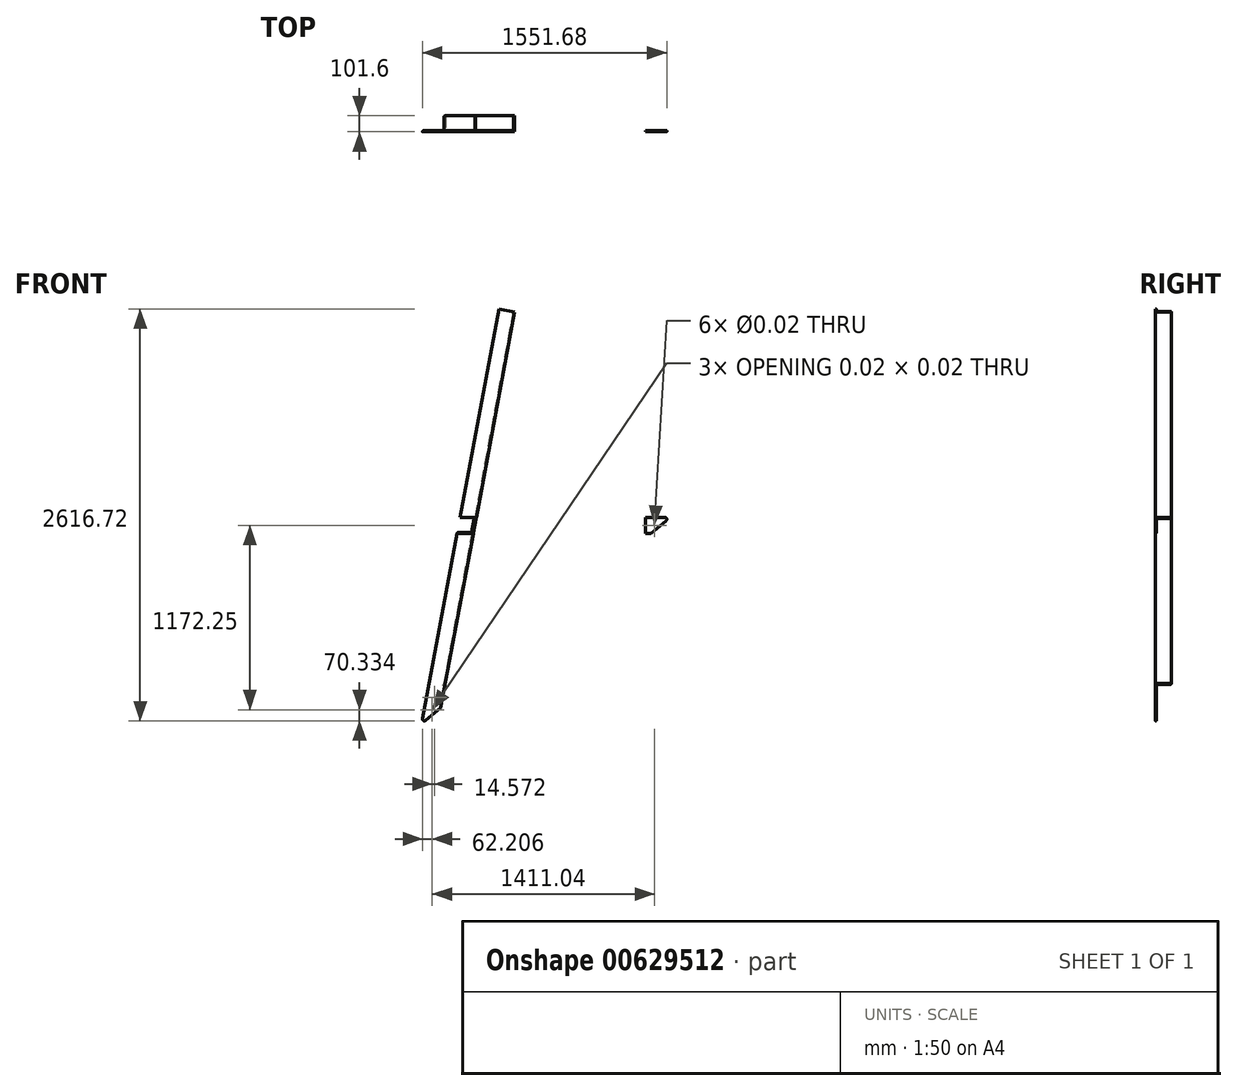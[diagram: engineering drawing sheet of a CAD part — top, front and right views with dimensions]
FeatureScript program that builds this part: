
annotation { "Feature Type Name" : "Feature", "Feature Type Description" : "" }
export const myFeature = defineFeature(function(context is Context, id is Id, definition is map)
    precondition{}
    {
        {
            var Q0;
            Q0=qCreatedBy(makeId("Front.planeOp"),FACE);
            var sketch = newSketch(context, id + "F0", { "sketchPlane" : qUnion([Q0])});
            skLineSegment(sketch, "E0", {"start": v(-1073.2, 0) * mm, "end": v(1073.2, 0) * mm, "construction": true});
            skLineSegment(sketch, "E1", {"start": v(-196.73, -1055.02) * mm, "end": v(196.73, 1055.02) * mm, "construction": true});
            skLineSegment(sketch, "E2", {"start": v(-1073.2, 0) * mm, "end": v(-196.73, -1055.02) * mm, "construction": true});
            skLineSegment(sketch, "E3", {"start": v(1073.2, 0) * mm, "end": v(-196.73, -1055.02) * mm, "construction": true});
            skLineSegment(sketch, "E4", {"start": v(1073.2, 0) * mm, "end": v(196.73, 1055.02) * mm, "construction": true});
            skLineSegment(sketch, "E5", {"start": v(-1073.2, 0) * mm, "end": v(196.73, 1055.02) * mm, "construction": true});
            skSolve(sketch);
        }
        {
            var Q0;
            Q0=sQuery(id+"F0.wireOp",VERTEX,"E3.start");
            var Q1;
            Q1=qCreatedBy(makeId("Right.planeOp"),FACE);
            cPlane(context, id + "F1", {"entities" : qUnion([Q0, Q1]), "cplaneType" : CPlaneType.PLANE_POINT, "offset" : 25.4 * mm, "width" : 152.4 * mm, "height" : 152.4 * mm});
        }
        {
            var Q0;
            Q0=qCreatedBy(id+"F1.planeOp",FACE);
            var sketch = newSketch(context, id + "F2", { "sketchPlane" : qUnion([Q0])});
            skLineSegment(sketch, "E6", {"start": v(-77.3, 0) * mm, "end": v(77.3, 0) * mm, "construction": true});
            skSolve(sketch);
        }
        {
            var Q0;
            Q0=qCreatedBy(id+"F1.planeOp",FACE);
            var sketch = newSketch(context, id + "F3", { "sketchPlane" : qUnion([Q0])});
            skLineSegment(sketch, "E7", {"start": v(0, 0) * mm, "end": v(101.6, 0) * mm});
            skLineSegment(sketch, "E8", {"start": v(101.6, 0) * mm, "end": v(101.6, -0.76) * mm});
            skLineSegment(sketch, "E9", {"start": v(96.01, -6.35) * mm, "end": v(11.94, -6.35) * mm});
            skLineSegment(sketch, "E10", {"start": v(6.35, -11.94) * mm, "end": v(6.35, -96.01) * mm});
            skLineSegment(sketch, "E11", {"start": v(0.76, -101.6) * mm, "end": v(0, -101.6) * mm});
            skLineSegment(sketch, "E12", {"start": v(0, -101.6) * mm, "end": v(0, 0) * mm});
            skPoint(sketch, "E13.visualSharp", {"position": v(6.35, -101.6) * mm});
            skArc(sketch, "E13.filletArc", {"start": v(0.76, -101.6) * mm, "mid": v(4.71, -99.96) * mm, "end": v(6.35, -96.01) * mm});
            skPoint(sketch, "E14.visualSharp", {"position": v(101.6, -6.35) * mm});
            skArc(sketch, "E14.filletArc", {"start": v(96.01, -6.35) * mm, "mid": v(99.96, -4.71) * mm, "end": v(101.6, -0.76) * mm});
            skPoint(sketch, "E15.visualSharp", {"position": v(6.35, -6.35) * mm});
            skArc(sketch, "E15.filletArc", {"start": v(11.94, -6.35) * mm, "mid": v(7.99, -7.99) * mm, "end": v(6.35, -11.94) * mm});
            skSolve(sketch);
        }
        {
            var Q0;
            Q0=makeQuery(id+"F3.imprint","IMPRINT",FACE,{"disambiguationData":[TD([[makeQuery(id+"F3.imprint","IMPRINT",EDGE,{"derivedFrom":sQuery(id+"F3.wireOp",EDGE,"E7")}),-1.0]])]});
            var Q1;
            Q1=sQuery(id+"F0.wireOp",VERTEX,"E0.start");
            extrude(context, id + "F4", {"entities" : qUnion([Q0]), "oppositeDirection" : true, "endBoundEntityVertex" : qUnion([Q1]), "depth" : 2540 * mm, "hasSecondDirection" : true, "secondDirectionOppositeDirection" : false, "secondDirectionDepth" : 254 * mm});
        }
        {
            var Q0;
            Q0=sQuery(id+"F0.wireOp",VERTEX,"E5.end");
            var Q1;
            Q1=sQuery(id+"F0.wireOp",EDGE,"E1");
            cPlane(context, id + "F5", {"entities" : qUnion([Q0, Q1]), "cplaneType" : CPlaneType.LINE_POINT, "offset" : 25.4 * mm, "width" : 152.4 * mm, "height" : 152.4 * mm});
        }
        {
            var Q0;
            Q0=qCreatedBy(id+"F5.planeOp",FACE);
            var sketch = newSketch(context, id + "F6", { "sketchPlane" : qUnion([Q0])});
            skLineSegment(sketch, "E16", {"start": v(0, 0) * mm, "end": v(0, 101.6) * mm});
            skLineSegment(sketch, "E17", {"start": v(0, 101.6) * mm, "end": v(-0.76, 101.6) * mm});
            skLineSegment(sketch, "E18", {"start": v(-6.35, 96.01) * mm, "end": v(-6.35, 11.94) * mm});
            skLineSegment(sketch, "E19", {"start": v(-11.94, 6.35) * mm, "end": v(-96.01, 6.35) * mm});
            skLineSegment(sketch, "E20", {"start": v(-101.6, 0.76) * mm, "end": v(-101.6, 0) * mm});
            skLineSegment(sketch, "E21", {"start": v(0, 0) * mm, "end": v(-101.6, 0) * mm});
            skPoint(sketch, "E22.visualSharp", {"position": v(-6.35, 101.6) * mm});
            skArc(sketch, "E22.filletArc", {"start": v(-0.76, 101.6) * mm, "mid": v(-4.71, 99.96) * mm, "end": v(-6.35, 96.01) * mm});
            skPoint(sketch, "E23.visualSharp", {"position": v(-6.35, 6.35) * mm});
            skArc(sketch, "E23.filletArc", {"start": v(-11.94, 6.35) * mm, "mid": v(-7.99, 7.99) * mm, "end": v(-6.35, 11.94) * mm});
            skPoint(sketch, "E24.visualSharp", {"position": v(-101.6, 6.35) * mm});
            skArc(sketch, "E24.filletArc", {"start": v(-96.01, 6.35) * mm, "mid": v(-99.96, 4.71) * mm, "end": v(-101.6, 0.76) * mm});
            skSolve(sketch);
        }
        {
            var Q0;
            Q0=makeQuery(id+"F6.imprint","IMPRINT",FACE,{"disambiguationData":[TD([[makeQuery(id+"F6.imprint","IMPRINT",EDGE,{"derivedFrom":sQuery(id+"F6.wireOp",EDGE,"E16")}),1.0]])]});
            extrude(context, id + "F7", {"entities" : qUnion([Q0]), "oppositeDirection" : true, "depth" : 2540 * mm, "hasSecondDirection" : true, "secondDirectionOppositeDirection" : false, "secondDirectionDepth" : 254 * mm});
        }
        {
            var Q0;
            Q0=qSketchRegion(id+"F3",true);
            extrude(context, id + "F8", {"entities" : qUnion([Q0]), "operationType" : NewBodyOperationType.REMOVE, "endBound" : BoundingType.THROUGH_ALL, "oppositeDirection" : true, "depth" : 25.4 * mm});
        }
        {
            var Q0;
            Q0=makeQuery(id+"F4.opExtrude","SWEPT_FACE",FACE,{"disambiguationData":[OSD([sQuery(id+"F3.wireOp",EDGE,"E10")])]});
            var sketch = newSketch(context, id + "F9", { "sketchPlane" : qUnion([Q0])});
            skLineSegment(sketch, "E25", {"start": v(-877.83, -162.31) * mm, "end": v(-1268.58, 162.31) * mm});
            skLineSegment(sketch, "E26", {"start": v(-1268.58, 162.31) * mm, "end": v(-1333.5, 84.16) * mm});
            skLineSegment(sketch, "E27", {"start": v(-1333.5, 84.16) * mm, "end": v(-942.76, -240.46) * mm});
            skLineSegment(sketch, "E28", {"start": v(-942.76, -240.46) * mm, "end": v(-877.83, -162.31) * mm});
            skSolve(sketch);
        }
        {
            var Q0;
            Q0=qSketchRegion(id+"F9",true);
            extrude(context, id + "F10", {"entities" : qUnion([Q0]), "operationType" : NewBodyOperationType.REMOVE, "endBound" : BoundingType.THROUGH_ALL, "depth" : 25.4 * mm});
        }
        {
            var Q0;
            Q0=makeQuery(id+"F4.opExtrude","SWEPT_FACE",FACE,{"disambiguationData":[OSD([sQuery(id+"F3.wireOp",EDGE,"E12")])]});
            var sketch = newSketch(context, id + "F11", { "sketchPlane" : qUnion([Q0])});
            skLineSegment(sketch, "E29", {"start": v(1333.5, 84.16) * mm, "end": v(942.76, -240.46) * mm});
            skLineSegment(sketch, "E30", {"start": v(942.76, -240.46) * mm, "end": v(1072.6, -396.76) * mm});
            skLineSegment(sketch, "E31", {"start": v(1072.6, -396.76) * mm, "end": v(1463.35, -72.14) * mm});
            skLineSegment(sketch, "E32", {"start": v(1463.35, -72.14) * mm, "end": v(1333.5, 84.16) * mm});
            skSolve(sketch);
        }
        {
            var Q0;
            Q0=qSketchRegion(id+"F11",true);
            extrude(context, id + "F12", {"entities" : qUnion([Q0]), "operationType" : NewBodyOperationType.REMOVE, "endBound" : BoundingType.THROUGH_ALL, "oppositeDirection" : true, "depth" : 25.4 * mm});
        }
        {
            var Q0;
            Q0=makeQuery(id+"F10.boolean.opBoolean","MERGE",FACE,{"derivedFrom":[makeQuery(id+"F4.opExtrude","SWEPT_FACE",FACE,{"disambiguationData":[OSD([sQuery(id+"F3.wireOp",EDGE,"E10")])]}),makeQuery(id+"F10.opExtrude","CAP_FACE",FACE,{"disambiguationData":[OSD([sQuery(id+"F9.wireOp",EDGE,"E25"),sQuery(id+"F9.wireOp",EDGE,"E26"),sQuery(id+"F9.wireOp",EDGE,"E27"),sQuery(id+"F9.wireOp",EDGE,"E28")])],"isStart":true})]});
            var sketch = newSketch(context, id + "F13", { "sketchPlane" : qUnion([Q0])});
            skLineSegment(sketch, "E33", {"start": v(-1131.3, -50.8) * mm, "end": v(-1051.8, -50.8) * mm, "construction": true});
            skSolve(sketch);
        }
        {
            var Q0;
            Q0=sQuery(id+"F13.wireOp",VERTEX,"E33.start");
            var Q1;
            Q1=sQuery(id+"F13.wireOp",VERTEX,"E33.end");
            var Q2;
            Q2=makeQuery(id+"F4.opExtrude","SWEPT_BODY",BODY,{"disambiguationData":[OSD([sQuery(id+"F3.wireOp",EDGE,"E7"),sQuery(id+"F3.wireOp",EDGE,"E8"),sQuery(id+"F3.wireOp",EDGE,"E9"),sQuery(id+"F3.wireOp",EDGE,"E10"),sQuery(id+"F3.wireOp",EDGE,"E11"),sQuery(id+"F3.wireOp",EDGE,"E12"),sQuery(id+"F3.wireOp",EDGE,"E13.filletArc"),sQuery(id+"F3.wireOp",EDGE,"E14.filletArc"),sQuery(id+"F3.wireOp",EDGE,"E15.filletArc")])]});
            var Q3;
            Q3=makeQuery(id+"F8.boolean.opBoolean","SPLIT",BODY,{"disambiguationData":[OD(0.0)],"derivedFrom":makeQuery(id+"F7.opExtrude","SWEPT_BODY",BODY,{"disambiguationData":[OSD([sQuery(id+"F6.wireOp",EDGE,"E16"),sQuery(id+"F6.wireOp",EDGE,"E17"),sQuery(id+"F6.wireOp",EDGE,"E18"),sQuery(id+"F6.wireOp",EDGE,"E19"),sQuery(id+"F6.wireOp",EDGE,"E20"),sQuery(id+"F6.wireOp",EDGE,"E21"),sQuery(id+"F6.wireOp",EDGE,"E22.filletArc"),sQuery(id+"F6.wireOp",EDGE,"E23.filletArc"),sQuery(id+"F6.wireOp",EDGE,"E24.filletArc")])]})});
            var Q4;
            Q4=makeQuery(id+"F8.boolean.opBoolean","SPLIT",BODY,{"disambiguationData":[OD(1.0)],"derivedFrom":makeQuery(id+"F7.opExtrude","SWEPT_BODY",BODY,{"disambiguationData":[OSD([sQuery(id+"F6.wireOp",EDGE,"E16"),sQuery(id+"F6.wireOp",EDGE,"E17"),sQuery(id+"F6.wireOp",EDGE,"E18"),sQuery(id+"F6.wireOp",EDGE,"E19"),sQuery(id+"F6.wireOp",EDGE,"E20"),sQuery(id+"F6.wireOp",EDGE,"E21"),sQuery(id+"F6.wireOp",EDGE,"E22.filletArc"),sQuery(id+"F6.wireOp",EDGE,"E23.filletArc"),sQuery(id+"F6.wireOp",EDGE,"E24.filletArc")])]})});
            hole(context, id + "F14", {"style" : HoleStyle.SIMPLE, "endStyle" : HoleEndStyle.THROUGH, "standardTappedOrClearance" : lookupTablePath({ "standard" : "ANSI", "size" : "9/16 (0.56)", "type" : "Drilled" }), "standardBlindInLast" : lookupTablePath({ "standard" : "ANSI", "size" : "9/16", "type" : "Drilled" }), "holeDiameter" : 9 / 406.4 * mm, "isTappedThrough" : true, "tappedDepth" : 12.7 * mm, "tapClearance" : 3, "locations" : qUnion([Q0, Q1]), "scope" : qUnion([Q2, Q3, Q4])});
        }
        {
            var Q0;
            Q0=sQuery(id+"F0.wireOp",EDGE,"E4");
            cPoint(context, id + "F15", {"entities" : qUnion([Q0]), "parameter" : 0.5});
        }
        {
            var Q0;
            Q0=qCreatedBy(id+"F15",VERTEX);
            var Q1;
            Q1=sQuery(id+"F0.wireOp",EDGE,"E4");
            cPlane(context, id + "F16", {"entities" : qUnion([Q0, Q1]), "cplaneType" : CPlaneType.LINE_POINT, "offset" : 25.4 * mm, "width" : 152.4 * mm, "height" : 152.4 * mm});
        }
        {
            var Q0;
            {var subQ2=sQuery(id+"F6.wireOp",EDGE,"E19");Q0=makeQuery(id+"F8.boolean.opBoolean","SPLIT",FACE,{"disambiguationData":[TD([makeQuery(id+"F8.opExtrude","SWEPT_FACE",FACE,{"disambiguationData":[OSD([sQuery(id+"F3.wireOp",EDGE,"E10")])]})])],"derivedFrom":makeQuery(id+"F7.opExtrude","SWEPT_FACE",FACE,{"disambiguationData":[OSD([subQ2])]})});}
            var sketch = newSketch(context, id + "F17", { "sketchPlane" : qUnion([Q0])});
            skLineSegment(sketch, "E34", {"start": v(196.73, -1055.02) * mm, "end": v(587.48, -1379.64) * mm});
            skLineSegment(sketch, "E35", {"start": v(587.48, -1379.64) * mm, "end": v(522.55, -1457.8) * mm});
            skLineSegment(sketch, "E36", {"start": v(522.55, -1457.8) * mm, "end": v(131.8, -1133.17) * mm});
            skLineSegment(sketch, "E37", {"start": v(131.8, -1133.17) * mm, "end": v(196.73, -1055.02) * mm});
            skSolve(sketch);
        }
        {
            var Q0;
            {var subQ1=sQuery(id+"F6.wireOp",EDGE,"E21");Q0=makeQuery(id+"F8.boolean.opBoolean","SPLIT",FACE,{"disambiguationData":[TD([makeQuery(id+"F8.opExtrude","SWEPT_FACE",FACE,{"disambiguationData":[OSD([sQuery(id+"F3.wireOp",EDGE,"E11")])]})])],"derivedFrom":makeQuery(id+"F7.opExtrude","SWEPT_FACE",FACE,{"disambiguationData":[OSD([subQ1])]})});}
            var sketch = newSketch(context, id + "F18", { "sketchPlane" : qUnion([Q0])});
            skLineSegment(sketch, "E38", {"start": v(-131.8, -1133.17) * mm, "end": v(-522.55, -1457.8) * mm});
            skLineSegment(sketch, "E39", {"start": v(-522.55, -1457.8) * mm, "end": v(-392.7, -1614.1) * mm});
            skLineSegment(sketch, "E40", {"start": v(-392.7, -1614.1) * mm, "end": v(-1.95, -1289.47) * mm});
            skLineSegment(sketch, "E41", {"start": v(-1.95, -1289.47) * mm, "end": v(-131.8, -1133.17) * mm});
            skSolve(sketch);
        }
        {
            var Q0;
            Q0=qSketchRegion(id+"F17",true);
            extrude(context, id + "F19", {"entities" : qUnion([Q0]), "operationType" : NewBodyOperationType.REMOVE, "endBound" : BoundingType.THROUGH_ALL, "depth" : 25.4 * mm});
        }
        {
            var Q0;
            Q0=qSketchRegion(id+"F18",true);
            extrude(context, id + "F20", {"entities" : qUnion([Q0]), "operationType" : NewBodyOperationType.REMOVE, "endBound" : BoundingType.THROUGH_ALL, "oppositeDirection" : true, "depth" : 25.4 * mm});
        }
        {
            var Q0;
            {var subQ2=sQuery(id+"F6.wireOp",EDGE,"E19");Q0=makeQuery(id+"F19.boolean.opBoolean","MERGE",FACE,{"derivedFrom":[makeQuery(id+"F8.boolean.opBoolean","SPLIT",FACE,{"disambiguationData":[TD([makeQuery(id+"F8.opExtrude","SWEPT_FACE",FACE,{"disambiguationData":[OSD([sQuery(id+"F3.wireOp",EDGE,"E10")])]})])],"derivedFrom":makeQuery(id+"F7.opExtrude","SWEPT_FACE",FACE,{"disambiguationData":[OSD([subQ2])]})}),makeQuery(id+"F19.opExtrude","CAP_FACE",FACE,{"disambiguationData":[OSD([sQuery(id+"F17.wireOp",EDGE,"E34"),sQuery(id+"F17.wireOp",EDGE,"E35"),sQuery(id+"F17.wireOp",EDGE,"E36"),sQuery(id+"F17.wireOp",EDGE,"E37")])],"isStart":true})]});}
            var sketch = newSketch(context, id + "F21", { "sketchPlane" : qUnion([Q0])});
            skLineSegment(sketch, "E42", {"start": v(279.73, -1223.05) * mm, "end": v(265.16, -1144.9) * mm, "construction": true});
            skSolve(sketch);
        }
        {
            var Q0;
            Q0=sQuery(id+"F21.wireOp",VERTEX,"E42.end");
            var Q1;
            Q1=sQuery(id+"F21.wireOp",VERTEX,"E42.start");
            var Q2;
            Q2=makeQuery(id+"F8.boolean.opBoolean","SPLIT",BODY,{"disambiguationData":[OD(1.0)],"derivedFrom":makeQuery(id+"F7.opExtrude","SWEPT_BODY",BODY,{"disambiguationData":[OSD([sQuery(id+"F6.wireOp",EDGE,"E16"),sQuery(id+"F6.wireOp",EDGE,"E17"),sQuery(id+"F6.wireOp",EDGE,"E18"),sQuery(id+"F6.wireOp",EDGE,"E19"),sQuery(id+"F6.wireOp",EDGE,"E20"),sQuery(id+"F6.wireOp",EDGE,"E21"),sQuery(id+"F6.wireOp",EDGE,"E22.filletArc"),sQuery(id+"F6.wireOp",EDGE,"E23.filletArc"),sQuery(id+"F6.wireOp",EDGE,"E24.filletArc")])]})});
            var Q3;
            Q3=makeQuery(id+"F4.opExtrude","SWEPT_BODY",BODY,{"disambiguationData":[OSD([sQuery(id+"F3.wireOp",EDGE,"E7"),sQuery(id+"F3.wireOp",EDGE,"E8"),sQuery(id+"F3.wireOp",EDGE,"E9"),sQuery(id+"F3.wireOp",EDGE,"E10"),sQuery(id+"F3.wireOp",EDGE,"E11"),sQuery(id+"F3.wireOp",EDGE,"E12"),sQuery(id+"F3.wireOp",EDGE,"E13.filletArc"),sQuery(id+"F3.wireOp",EDGE,"E14.filletArc"),sQuery(id+"F3.wireOp",EDGE,"E15.filletArc")])]});
            hole(context, id + "F22", {"style" : HoleStyle.SIMPLE, "endStyle" : HoleEndStyle.THROUGH, "standardTappedOrClearance" : lookupTablePath({ "standard" : "ANSI", "size" : "9/16 (0.56)", "type" : "Drilled" }), "standardBlindInLast" : lookupTablePath({ "standard" : "ANSI", "size" : "9/16", "type" : "Drilled" }), "holeDiameter" : 9 / 406.4 * mm, "isTappedThrough" : true, "tappedDepth" : 12.7 * mm, "tapClearance" : 3, "locations" : qUnion([Q0, Q1]), "scope" : qUnion([Q2, Q3])});
        }
        {
            var Q0;
            {var subQ2=sQuery(id+"F6.wireOp",EDGE,"E19");Q0=makeQuery(id+"F19.boolean.opBoolean","MERGE",FACE,{"derivedFrom":[makeQuery(id+"F8.boolean.opBoolean","SPLIT",FACE,{"disambiguationData":[TD([makeQuery(id+"F8.opExtrude","SWEPT_FACE",FACE,{"disambiguationData":[OSD([sQuery(id+"F3.wireOp",EDGE,"E10")])]})])],"derivedFrom":makeQuery(id+"F7.opExtrude","SWEPT_FACE",FACE,{"disambiguationData":[OSD([subQ2])]})}),makeQuery(id+"F19.opExtrude","CAP_FACE",FACE,{"disambiguationData":[OSD([sQuery(id+"F17.wireOp",EDGE,"E34"),sQuery(id+"F17.wireOp",EDGE,"E35"),sQuery(id+"F17.wireOp",EDGE,"E36"),sQuery(id+"F17.wireOp",EDGE,"E37")])],"isStart":true})]});}
            var sketch = newSketch(context, id + "F23", { "sketchPlane" : qUnion([Q0])});
            skLineSegment(sketch, "E43", {"start": v(348.17, -1312.92) * mm, "end": v(321.12, -1290.45) * mm});
            skLineSegment(sketch, "E44", {"start": v(348.17, -1312.92) * mm, "end": v(341.72, -1278.36) * mm});
            skPoint(sketch, "E45.visualSharp", {"position": v(348.17, -1312.92) * mm});
            skArc(sketch, "E45.filletArc", {"start": v(321.12, -1290.45) * mm, "mid": v(335.67, -1291.64) * mm, "end": v(341.72, -1278.36) * mm});
            skSolve(sketch);
        }
        {
            var Q0;
            Q0=qSketchRegion(id+"F23",true);
            extrude(context, id + "F24", {"entities" : qUnion([Q0]), "operationType" : NewBodyOperationType.REMOVE, "endBound" : BoundingType.THROUGH_ALL, "oppositeDirection" : true, "depth" : 25.4 * mm});
        }
        {
            var Q0;
            Q0=makeQuery(id+"F12.boolean.opBoolean","INTERSECT",EDGE,{"derivedFrom":[makeQuery(id+"F4.opExtrude","SWEPT_FACE",FACE,{"disambiguationData":[OSD([sQuery(id+"F3.wireOp",EDGE,"E7")])]}),makeQuery(id+"F12.opExtrude","SWEPT_FACE",FACE,{"disambiguationData":[OSD([sQuery(id+"F11.wireOp",EDGE,"E29")])]})]});
            var Q1;
            {var subQ2=sQuery(id+"F6.wireOp",EDGE,"E16");Q1=makeQuery(id+"FlhLudVOjt02WCi_2.1.F12.boolean.opBoolean","INTERSECT",EDGE,{"derivedFrom":[makeQuery(id+"F8.boolean.opBoolean","SPLIT",FACE,{"disambiguationData":[TD([makeQuery(id+"F8.opExtrude","SWEPT_FACE",FACE,{"disambiguationData":[OSD([sQuery(id+"F3.wireOp",EDGE,"E7")])]})])],"derivedFrom":makeQuery(id+"F7.opExtrude","SWEPT_FACE",FACE,{"disambiguationData":[OSD([subQ2])]})}),makeQuery(id+"FlhLudVOjt02WCi_2.1.F12.opExtrude","SWEPT_FACE",FACE,{"disambiguationData":[OSD([sQuery(id+"F11.wireOp",EDGE,"E29")])]})]});}
            fillet(context, id + "F25", {"entities" : qUnion([Q0, Q1]), "radius" : 12.7 * mm, "tangentPropagation" : true, "allowEdgeOverflow" : false});
        }
    });
